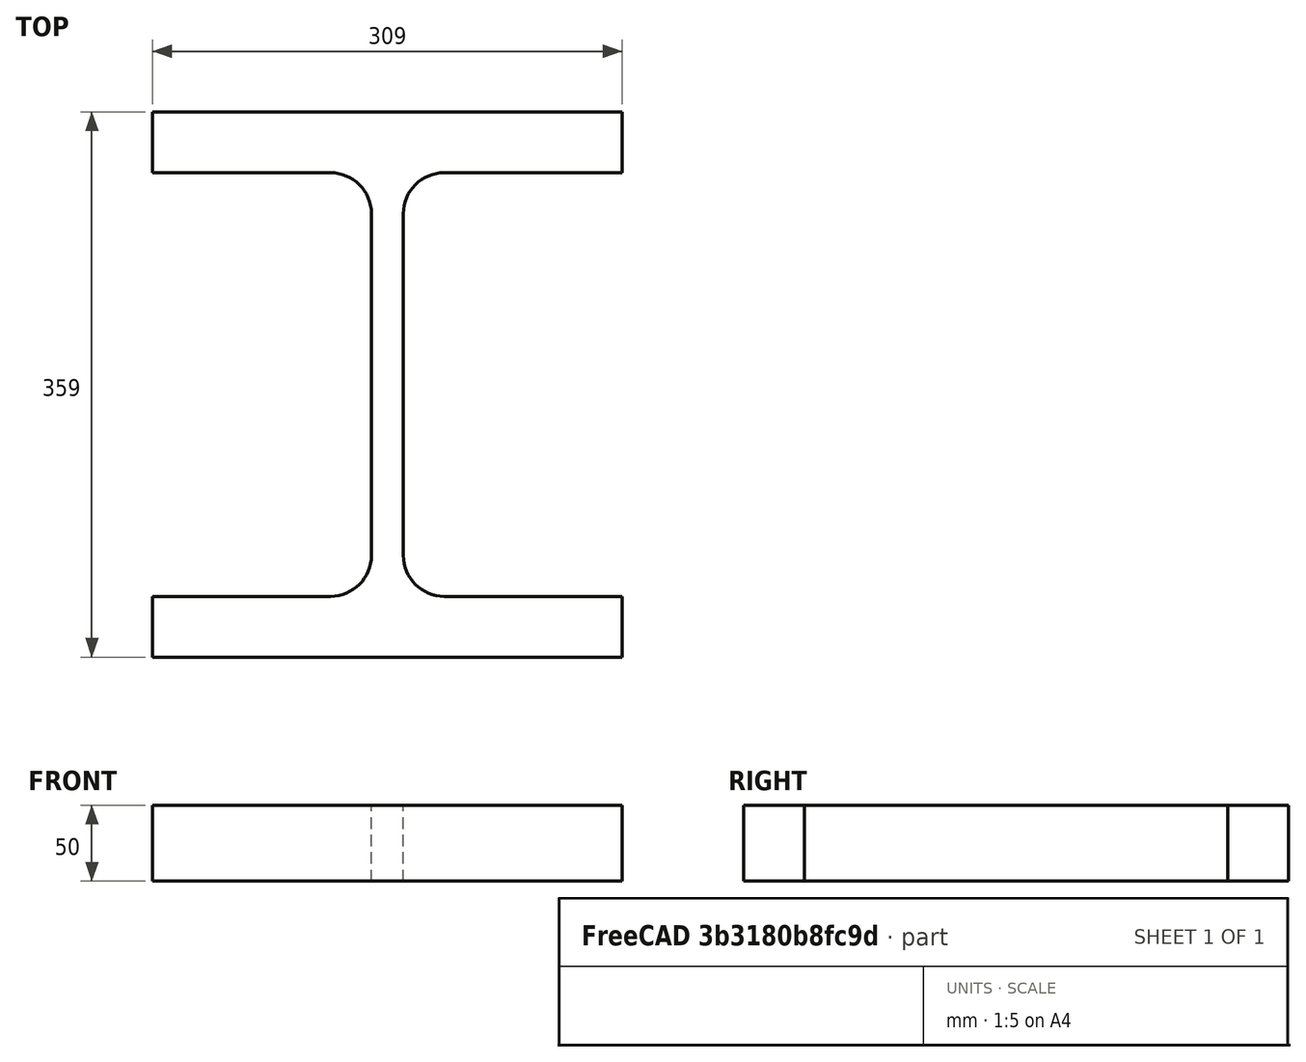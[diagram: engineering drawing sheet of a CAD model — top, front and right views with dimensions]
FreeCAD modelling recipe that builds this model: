
FCSTD DOCUMENT  (FreeCAD 0.15R4671 (Git))
Label: HE-M-Profile 320 DIN1025-4 S235JR
License: All rights reserved
LicenseURL: http://en.wikipedia.org/wiki/All_rights_reserved
objects: Sketcher::SketchObject×1, Part::Extrusion×1
note: 2 computed .brp shape members not serialized (recipe doc carries the construction recipe); baked Part::Feature solids carry a one-line shape summary decoded from their .brp

FEATURE [Sketcher::SketchObject] Sketch
  sketch-geometry (16):
    g0: LineSegment StartX=10.5 StartY=-112.5 StartZ=0 EndX=10.5 EndY=112.5 EndZ=0
    g1: LineSegment StartX=37.5 StartY=139.5 StartZ=0 EndX=154.5 EndY=139.5 EndZ=0
    g2: LineSegment StartX=154.5 StartY=139.5 StartZ=0 EndX=154.5 EndY=179.5 EndZ=0
    g3: LineSegment StartX=154.5 StartY=179.5 StartZ=0 EndX=-154.5 EndY=179.5 EndZ=0
    g4: LineSegment StartX=-154.5 StartY=179.5 StartZ=0 EndX=-154.5 EndY=139.5 EndZ=0
    g5: LineSegment StartX=-154.5 StartY=139.5 StartZ=0 EndX=-37.5 EndY=139.5 EndZ=0
    g6: LineSegment StartX=-10.5 StartY=112.5 StartZ=0 EndX=-10.5 EndY=-112.5 EndZ=0
    g7: LineSegment StartX=-37.5 StartY=-139.5 StartZ=0 EndX=-154.5 EndY=-139.5 EndZ=0
    g8: LineSegment StartX=-154.5 StartY=-139.5 StartZ=0 EndX=-154.5 EndY=-179.5 EndZ=0
    g9: LineSegment StartX=-154.5 StartY=-179.5 StartZ=0 EndX=154.5 EndY=-179.5 EndZ=0
    g10: LineSegment StartX=154.5 StartY=-179.5 StartZ=0 EndX=154.5 EndY=-139.5 EndZ=0
    g11: LineSegment StartX=154.5 StartY=-139.5 StartZ=0 EndX=37.5 EndY=-139.5 EndZ=0
    g12: ArcOfCircle CenterX=37.5 CenterY=112.5 CenterZ=0 NormalX=0 NormalY=0 NormalZ=1 Radius=27 StartAngle=1.5708 EndAngle=3.14159
    g13: ArcOfCircle CenterX=37.5 CenterY=-112.5 CenterZ=0 NormalX=0 NormalY=0 NormalZ=1 Radius=27 StartAngle=3.14159 EndAngle=4.71239
    g14: ArcOfCircle CenterX=-37.5 CenterY=112.5 CenterZ=0 NormalX=0 NormalY=0 NormalZ=1 Radius=27 StartAngle=0 EndAngle=1.5708
    g15: ArcOfCircle CenterX=-37.5 CenterY=-112.5 CenterZ=0 NormalX=0 NormalY=0 NormalZ=1 Radius=27 StartAngle=4.71239 EndAngle=6.28319
  constraints (42):
    c: Vertical(g0)
    c: Coincident(g2,g1)
    c: Vertical(g2)
    c: Coincident(g3,g2)
    c: Coincident(g4,g3)
    c: Vertical(g4)
    c: Coincident(g5,g4)
    c: Horizontal(g5)
    c: Vertical(g6)
    c: Horizontal(g7)
    c: Coincident(g8,g7)
    c: Vertical(g8)
    c: Coincident(g9,g8)
    c: Horizontal(g9)
    c: Coincident(g10,g9)
    c: Vertical(g10)
    c: Coincident(g11,g10)
    c: Horizontal(g11)
    c: Tangent(g1,g12) = 1.5708
    c: Tangent(g0,g12) = 1.5708
    c: Tangent(g0,g13) = 1.5708
    c: Tangent(g11,g13) = 1.5708
    c: Tangent(g5,g14) = 1.5708
    c: Tangent(g6,g14) = 1.5708
    c: Tangent(g6,g15) = 1.5708
    c: Tangent(g7,g15) = 1.5708
    c: Equal(g3,g9)
    c: Equal(g2,g4)
    c: Equal(g4,g8)
    c: Equal(g8,g10)
    c: Equal(g12,g14)
    c: Equal(g14,g15)
    c: Equal(g15,g13)
    c: Symmetric(g2,g3,g-2)
    c: Symmetric(g9,g8,g-2)
    c: Symmetric(g0,g6,g-2)
    c: Symmetric(g2,g9,g-1)
    c: DistanceY(g2,g9) = -359
    c: DistanceX(g3) = -309
    c: DistanceX(g0,g6) = -21
    c: DistanceY(g2) = 40
    c: Radius(g12) = 27
FEATURE [Part::Extrusion] Extrude  label="HE-M-Profile 320 DIN1025-4 S235JR"
  Base = -> Sketch
  Dir = (0,0,50)
  Solid = true
